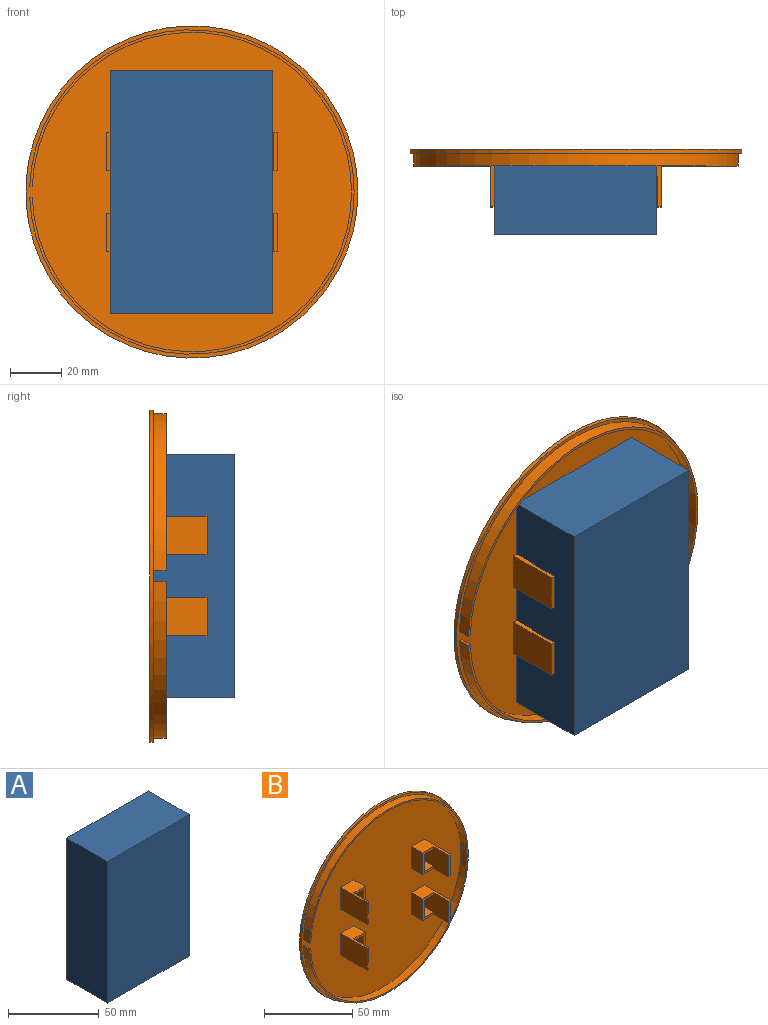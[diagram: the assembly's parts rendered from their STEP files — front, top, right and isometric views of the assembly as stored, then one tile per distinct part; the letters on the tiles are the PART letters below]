
ASSEMBLY  parts=2 mates=1
PART A: 6 faces, bbox 63.5x31.8x95.3 mm
  f0: plane 63.5x31.75mm, normal (0,0,-1), area 2016.1mm2, adj f1,f3,f4,f5
  f1: plane 95.25x31.75mm, normal (1,0,0), area 3024.2mm2, adj f0,f2,f4,f5
  f2: plane 63.5x31.75mm, normal (0,0,1), area 2016.1mm2, adj f1,f3,f4,f5
  f3: plane 95.25x31.75mm, normal (-1,0,0), area 3024.2mm2, adj f0,f2,f4,f5
  f4: plane 95.25x63.5mm, normal (0,-1,0), area 6048.4mm2, adj f0,f1,f2,f3
  f5: plane 95.25x63.5mm, normal (0,1,0), area 6048.4mm2, adj f0,f1,f2,f3
PART B: 52 faces, bbox 130x22.5x130 mm
  f0: plane 12x7.5mm, normal (0,-1,0), area 90mm2, adj f33,f34,f35,f49
  f1: plane 130x130mm, normal (0,-1,0), area 12251.6mm2, adj f5,f7,f8,f9,f10,f13,f14,f15
  f2: plane 12x7.5mm, normal (0,-1,0), area 90mm2, adj f26,f30,f31,f46
  f3: plane 12x7.5mm, normal (0,-1,0), area 90mm2, adj f12,f16,f17,f40
  f4: plane 12x7.5mm, normal (0,-1,0), area 90mm2, adj f22,f23,f24,f43
  f5: cylinder r=65mm len=130mm, axis (0,-1,0), area 612.6mm2, adj f1,f6
  f6: plane 130x130mm, normal (0,1,0), area 13273.2mm2, adj f5
  f7: cylinder r=63.5mm len=127mm, axis (0,1,0), area 1973.7mm2, adj f1,f8,f10,f11
  f8: plane 5x1mm, normal (0,0,-1), area 5mm2, adj f1,f7,f9,f11
  f9: cylinder r=62.5mm len=125mm, axis (0,1,0), area 1942.3mm2, adj f1,f8,f10,f11
  f10: plane 5x1mm, normal (0,0,1), area 5mm2, adj f1,f7,f9,f11
  f11: plane 127x126.96mm, normal (0,-1,0), area 391.6mm2, adj f7,f8,f9,f10
  f12: plane 9x7.5mm, normal (0,0,-1), area 67.5mm2, adj f3,f17,f18,f40
  f13: plane 21x10.5mm, normal (0,0,1), area 112.5mm2, adj f1,f14,f18,f40,f41,f42
  f14: plane 15x9mm, normal (-1,0,0), area 135mm2, adj f1,f13,f15,f18
  f15: plane 21x10.5mm, normal (0,0,-1), area 112.5mm2, adj f1,f14,f18,f40,f41,f42
  f16: plane 9x7.5mm, normal (0,0,1), area 67.5mm2, adj f3,f17,f18,f40
  f17: plane 12x9mm, normal (1,0,0), area 108mm2, adj f3,f12,f16,f18
  f18: plane 15x9mm, normal (0,-1,0), area 45mm2, adj f12,f13,f14,f15,f16,f17,f40
  f19: plane 21x10.5mm, normal (0,0,-1), area 112.5mm2, adj f1,f20,f25,f43,f44,f45
  f20: plane 15x9mm, normal (1,0,0), area 135mm2, adj f1,f19,f21,f25
  f21: plane 21x10.5mm, normal (0,0,1), area 112.5mm2, adj f1,f20,f25,f43,f44,f45
  f22: plane 9x7.5mm, normal (0,0,-1), area 67.5mm2, adj f4,f23,f25,f43
  f23: plane 12x9mm, normal (-1,0,0), area 108mm2, adj f4,f22,f24,f25
  f24: plane 9x7.5mm, normal (0,0,1), area 67.5mm2, adj f4,f23,f25,f43
  f25: plane 15x9mm, normal (0,-1,0), area 45mm2, adj f19,f20,f21,f22,f23,f24,f43
  f26: plane 9x7.5mm, normal (0,0,1), area 67.5mm2, adj f2,f31,f32,f46
  f27: plane 21x10.5mm, normal (0,0,-1), area 112.5mm2, adj f1,f28,f32,f46,f47,f48
  f28: plane 15x9mm, normal (1,0,0), area 135mm2, adj f1,f27,f29,f32
  f29: plane 21x10.5mm, normal (0,0,1), area 112.5mm2, adj f1,f28,f32,f46,f47,f48
  f30: plane 9x7.5mm, normal (0,0,-1), area 67.5mm2, adj f2,f31,f32,f46
  f31: plane 12x9mm, normal (-1,0,0), area 108mm2, adj f2,f26,f30,f32
  f32: plane 15x9mm, normal (0,-1,0), area 45mm2, adj f26,f27,f28,f29,f30,f31,f46
  f33: plane 9x7.5mm, normal (0,0,1), area 67.5mm2, adj f0,f34,f39,f49
  f34: plane 12x9mm, normal (1,0,0), area 108mm2, adj f0,f33,f35,f39
  f35: plane 9x7.5mm, normal (0,0,-1), area 67.5mm2, adj f0,f34,f39,f49
  f36: plane 21x10.5mm, normal (0,0,1), area 112.5mm2, adj f1,f37,f39,f49,f50,f51
  f37: plane 15x9mm, normal (-1,0,0), area 135mm2, adj f1,f36,f38,f39
  f38: plane 21x10.5mm, normal (0,0,-1), area 112.5mm2, adj f1,f37,f39,f49,f50,f51
  f39: plane 15x9mm, normal (0,-1,0), area 45mm2, adj f33,f34,f35,f36,f37,f38,f49
  f40: plane 21x15mm, normal (-1,0,0), area 288mm2, adj f3,f12,f13,f15,f16,f18,f42
  f41: plane 21x15mm, normal (1,0,0), area 315mm2, adj f1,f13,f15,f42
  f42: plane 15x1.5mm, normal (0,-1,0), area 22.5mm2, adj f13,f15,f40,f41
  f43: plane 21x15mm, normal (1,0,0), area 288mm2, adj f4,f19,f21,f22,f24,f25,f45
  f44: plane 21x15mm, normal (-1,0,0), area 315mm2, adj f1,f19,f21,f45
  f45: plane 15x1.5mm, normal (0,-1,0), area 22.5mm2, adj f19,f21,f43,f44
  f46: plane 21x15mm, normal (1,0,0), area 288mm2, adj f2,f26,f27,f29,f30,f32,f48
  f47: plane 21x15mm, normal (-1,0,0), area 315mm2, adj f1,f27,f29,f48
  f48: plane 15x1.5mm, normal (0,-1,0), area 22.5mm2, adj f27,f29,f46,f47
  f49: plane 21x15mm, normal (-1,0,0), area 288mm2, adj f0,f33,f35,f36,f38,f39,f51
  f50: plane 21x15mm, normal (1,0,0), area 315mm2, adj f1,f36,f38,f51
  f51: plane 15x1.5mm, normal (0,-1,0), area 22.5mm2, adj f36,f38,f49,f50
PLACE A rot(axis=(1,0,0),180deg) t=(-0.02,-31.75,0)mm
PLACE B at identity
MATE fastened A.f4 <-> B.f1  axis (0,1,0) through (-0.02,0,0)mm
